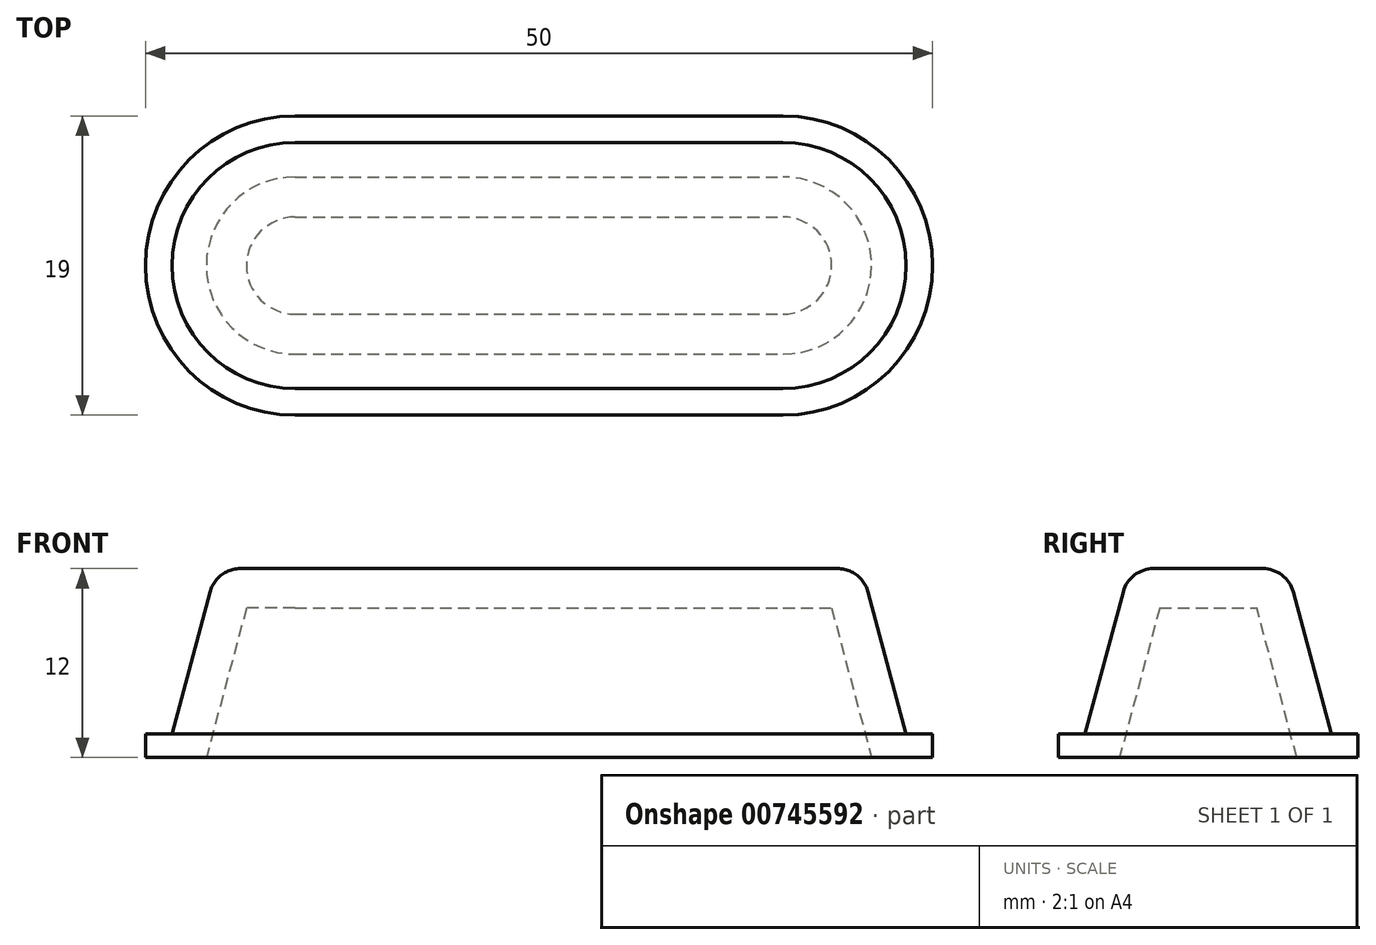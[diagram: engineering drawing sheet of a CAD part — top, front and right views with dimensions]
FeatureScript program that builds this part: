
annotation { "Feature Type Name" : "Feature", "Feature Type Description" : "" }
export const myFeature = defineFeature(function(context is Context, id is Id, definition is map)
    precondition{}
    {
        {
            var Q0;
            Q0=qCreatedBy(makeId("Top.planeOp"),FACE);
            var sketch = newSketch(context, id + "F0", { "sketchPlane" : qUnion([Q0])});
            skLineSegment(sketch, "E0.bottom", {"start": v(25, -9.5) * mm, "end": v(-25, -9.5) * mm, "construction": true});
            skLineSegment(sketch, "E0.top", {"start": v(25, 9.5) * mm, "end": v(-25, 9.5) * mm, "construction": true});
            skLineSegment(sketch, "E0.left", {"start": v(25, -9.5) * mm, "end": v(25, 9.5) * mm, "construction": true});
            skLineSegment(sketch, "E0.right", {"start": v(-25, -9.5) * mm, "end": v(-25, 9.5) * mm, "construction": true});
            skPoint(sketch, "E0.middle", {"position": v(0, 0) * mm});
            skLineSegment(sketch, "E1.bottom", {"start": v(23.5, -8) * mm, "end": v(-23.5, -8) * mm, "construction": true});
            skLineSegment(sketch, "E1.top", {"start": v(23.5, 8) * mm, "end": v(-23.5, 8) * mm, "construction": true});
            skLineSegment(sketch, "E1.left", {"start": v(23.5, -8) * mm, "end": v(23.5, 8) * mm, "construction": true});
            skLineSegment(sketch, "E1.right", {"start": v(-23.5, -8) * mm, "end": v(-23.5, 8) * mm, "construction": true});
            skLineSegment(sketch, "E2", {"start": v(0, 0) * mm, "end": v(-15.5, 0) * mm, "construction": true});
            skLineSegment(sketch, "E3", {"start": v(-15.5, 0) * mm, "end": v(0, 0) * mm, "construction": true});
            skLineSegment(sketch, "E4", {"start": v(0, 0) * mm, "end": v(15.5, 0) * mm, "construction": true});
            skCircle(sketch, "E5", {"center": v(-15.5, 0) * mm, "radius": 8 * mm, "construction": true});
            skCircle(sketch, "E6", {"center": v(15.5, 0) * mm, "radius": 8 * mm, "construction": true});
            skArc(sketch, "E7", {"start": v(-15.5, -8) * mm, "mid": v(-23.5, 0) * mm, "end": v(-15.5, 8) * mm, "construction": true});
            skArc(sketch, "E8", {"start": v(15.5, -8) * mm, "mid": v(23.5, 0) * mm, "end": v(15.5, 8) * mm, "construction": true});
            skLineSegment(sketch, "E9", {"start": v(-15.5, 8) * mm, "end": v(15.5, 8) * mm, "construction": true});
            skLineSegment(sketch, "E10", {"start": v(-15.5, -8) * mm, "end": v(15.5, -8) * mm, "construction": true});
            skArc(sketch, "E11", {"start": v(-15.5, 8) * mm, "mid": v(-23.5, 0) * mm, "end": v(-15.5, -8) * mm});
            skArc(sketch, "E12", {"start": v(15.5, 8) * mm, "mid": v(23.5, 0) * mm, "end": v(15.5, -8) * mm});
            skLineSegment(sketch, "E13", {"start": v(-15.5, -8) * mm, "end": v(15.5, -8) * mm});
            skLineSegment(sketch, "E14", {"start": v(-15.5, 8) * mm, "end": v(15.5, 8) * mm});
            skCircle(sketch, "E15", {"center": v(-15.5, 0) * mm, "radius": 9.5 * mm, "construction": true});
            skCircle(sketch, "E16", {"center": v(15.5, 0) * mm, "radius": 9.5 * mm, "construction": true});
            skArc(sketch, "E17", {"start": v(-15.5, 9.5) * mm, "mid": v(-25, 0) * mm, "end": v(-15.5, -9.5) * mm, "construction": true});
            skArc(sketch, "E18", {"start": v(15.5, 9.5) * mm, "mid": v(25, 0) * mm, "end": v(15.5, -9.5) * mm, "construction": true});
            skArc(sketch, "E19", {"start": v(-15.5, 9.5) * mm, "mid": v(-25, 0) * mm, "end": v(-15.5, -9.5) * mm});
            skArc(sketch, "E20", {"start": v(15.5, 9.5) * mm, "mid": v(25, 0) * mm, "end": v(15.5, -9.5) * mm});
            skLineSegment(sketch, "E21", {"start": v(-15.5, 9.5) * mm, "end": v(15.5, 9.5) * mm});
            skLineSegment(sketch, "E22", {"start": v(-15.5, -9.5) * mm, "end": v(15.5, -9.5) * mm});
            skSolve(sketch);
        }
        {
            var Q0;
            Q0=makeQuery(id+"F0.imprint","IMPRINT",FACE,{"disambiguationData":[TD([[makeQuery(id+"F0.imprint","IMPRINT",EDGE,{"derivedFrom":sQuery(id+"F0.wireOp",EDGE,"E11")}),-1.0]])]});
            var Q1;
            Q1=makeQuery(id+"F0.imprint","IMPRINT",FACE,{"disambiguationData":[TD([[makeQuery(id+"F0.imprint","IMPRINT",EDGE,{"derivedFrom":sQuery(id+"F0.wireOp",EDGE,"E11")}),1.0]])]});
            extrude(context, id + "F1", {"entities" : qUnion([Q0, Q1]), "oppositeDirection" : true, "depth" : 1.5 * mm, "offsetDistance" : 25 * mm});
        }
        {
            var Q0;
            Q0=makeQuery(id+"F1.opExtrude","CAP_FACE",FACE,{"disambiguationData":[OSD([sQuery(id+"F0.wireOp",EDGE,"E19"),sQuery(id+"F0.wireOp",EDGE,"E20"),sQuery(id+"F0.wireOp",EDGE,"E21"),sQuery(id+"F0.wireOp",EDGE,"E22")])],"isStart":true});
            var sketch = newSketch(context, id + "F2", { "sketchPlane" : qUnion([Q0])});
            skLineSegment(sketch, "E23.bottom", {"start": v(25, -9.5) * mm, "end": v(-25, -9.5) * mm, "construction": true});
            skLineSegment(sketch, "E23.top", {"start": v(25, 9.5) * mm, "end": v(-25, 9.5) * mm, "construction": true});
            skLineSegment(sketch, "E23.left", {"start": v(25, -9.5) * mm, "end": v(25, 9.5) * mm, "construction": true});
            skLineSegment(sketch, "E23.right", {"start": v(-25, -9.5) * mm, "end": v(-25, 9.5) * mm, "construction": true});
            skPoint(sketch, "E23.middle", {"position": v(0, 0) * mm});
            skLineSegment(sketch, "E24.bottom", {"start": v(23.5, -8) * mm, "end": v(-23.5, -8) * mm, "construction": true});
            skLineSegment(sketch, "E24.top", {"start": v(23.5, 8) * mm, "end": v(-23.5, 8) * mm, "construction": true});
            skLineSegment(sketch, "E24.left", {"start": v(23.5, -8) * mm, "end": v(23.5, 8) * mm, "construction": true});
            skLineSegment(sketch, "E24.right", {"start": v(-23.5, -8) * mm, "end": v(-23.5, 8) * mm, "construction": true});
            skLineSegment(sketch, "E25", {"start": v(0, 0) * mm, "end": v(-15.5, 0) * mm, "construction": true});
            skLineSegment(sketch, "E26", {"start": v(-15.5, 0) * mm, "end": v(0, 0) * mm, "construction": true});
            skLineSegment(sketch, "E27", {"start": v(0, 0) * mm, "end": v(15.5, 0) * mm, "construction": true});
            skCircle(sketch, "E28", {"center": v(-15.5, 0) * mm, "radius": 8 * mm, "construction": true});
            skCircle(sketch, "E29", {"center": v(15.5, 0) * mm, "radius": 8 * mm, "construction": true});
            skArc(sketch, "E30", {"start": v(-15.5, -8) * mm, "mid": v(-23.5, 0) * mm, "end": v(-15.5, 8) * mm, "construction": true});
            skArc(sketch, "E31", {"start": v(15.5, -8) * mm, "mid": v(23.5, 0) * mm, "end": v(15.5, 8) * mm, "construction": true});
            skLineSegment(sketch, "E32", {"start": v(-15.5, 8) * mm, "end": v(15.5, 8) * mm, "construction": true});
            skLineSegment(sketch, "E33", {"start": v(-15.5, -8) * mm, "end": v(15.5, -8) * mm, "construction": true});
            skArc(sketch, "E34", {"start": v(-15.5, 8) * mm, "mid": v(-23.5, 0) * mm, "end": v(-15.5, -8) * mm});
            skArc(sketch, "E35", {"start": v(15.5, 8) * mm, "mid": v(23.5, 0) * mm, "end": v(15.5, -8) * mm});
            skLineSegment(sketch, "E36", {"start": v(-15.5, -8) * mm, "end": v(15.5, -8) * mm});
            skLineSegment(sketch, "E37", {"start": v(-15.5, 8) * mm, "end": v(15.5, 8) * mm});
            skCircle(sketch, "E38", {"center": v(-15.5, 0) * mm, "radius": 9.5 * mm, "construction": true});
            skCircle(sketch, "E39", {"center": v(15.5, 0) * mm, "radius": 9.5 * mm, "construction": true});
            skArc(sketch, "E40", {"start": v(-15.5, 9.5) * mm, "mid": v(-25, 0) * mm, "end": v(-15.5, -9.5) * mm, "construction": true});
            skArc(sketch, "E41", {"start": v(15.5, 9.5) * mm, "mid": v(25, 0) * mm, "end": v(15.5, -9.5) * mm, "construction": true});
            skArc(sketch, "E42", {"start": v(-15.5, 9.5) * mm, "mid": v(-25, 0) * mm, "end": v(-15.5, -9.5) * mm});
            skArc(sketch, "E43", {"start": v(15.5, 9.5) * mm, "mid": v(25, 0) * mm, "end": v(15.5, -9.5) * mm});
            skLineSegment(sketch, "E44", {"start": v(-15.5, 9.5) * mm, "end": v(15.5, 9.5) * mm});
            skLineSegment(sketch, "E45", {"start": v(-15.5, -9.5) * mm, "end": v(15.5, -9.5) * mm});
            skSolve(sketch);
        }
        {
            var Q0;
            Q0=makeQuery(id+"F2.imprint","IMPRINT",FACE,{"disambiguationData":[TD([[makeQuery(id+"F2.imprint","IMPRINT",EDGE,{"derivedFrom":sQuery(id+"F2.wireOp",EDGE,"E34")}),1.0]])]});
            extrude(context, id + "F3", {"entities" : qUnion([Q0]), "operationType" : NewBodyOperationType.ADD, "depth" : 10.5 * mm, "offsetDistance" : 25 * mm});
        }
        {
            var Q0;
            Q0=makeQuery(id+"F3.opExtrude","CAP_FACE",FACE,{"disambiguationData":[OSD([sQuery(id+"F2.wireOp",EDGE,"E34"),sQuery(id+"F2.wireOp",EDGE,"E35"),sQuery(id+"F2.wireOp",EDGE,"E36"),sQuery(id+"F2.wireOp",EDGE,"E37")])],"isStart":false});
            chamfer(context, id + "F4", {"entities" : qUnion([Q0]), "chamferType" : ChamferType.OFFSET_ANGLE, "width" : 3 * mm, "oppositeDirection" : false, "angle" : 75 * degree, "tangentPropagation" : true});
        }
        {
            var Q0;
            Q0=makeQuery(id+"F1.opExtrude","CAP_FACE",FACE,{"disambiguationData":[OSD([sQuery(id+"F0.wireOp",EDGE,"E19"),sQuery(id+"F0.wireOp",EDGE,"E20"),sQuery(id+"F0.wireOp",EDGE,"E21"),sQuery(id+"F0.wireOp",EDGE,"E22")])],"isStart":false});
            shell(context, id + "F5", {"entities" : qUnion([Q0]), "thickness" : 2.5 * mm});
        }
        {
            var Q0;
            {var subQ0=sQuery(id+"F2.wireOp",EDGE,"E34");Q0=makeQuery(id+"F4.opChamfer","BLEND_EDGE",EDGE,{"blendedFrom":[makeQuery(id+"F3.opExtrude","CAP_EDGE",EDGE,{"disambiguationData":[OSD([subQ0])],"isStart":false}),makeQuery(id+"F3.opExtrude","CAP_FACE",FACE,{"disambiguationData":[OSD([subQ0,sQuery(id+"F2.wireOp",EDGE,"E35"),sQuery(id+"F2.wireOp",EDGE,"E36"),sQuery(id+"F2.wireOp",EDGE,"E37")])],"isStart":false})],"blendedInto":[makeQuery(id+"F3.opExtrude","CAP_FACE",FACE,{"disambiguationData":[OSD([subQ0,sQuery(id+"F2.wireOp",EDGE,"E35"),sQuery(id+"F2.wireOp",EDGE,"E36"),sQuery(id+"F2.wireOp",EDGE,"E37")])],"isStart":false})]});}
            fillet(context, id + "F6", {"entities" : qUnion([Q0]), "radius" : 2 * mm, "tangentPropagation" : true, "allowEdgeOverflow" : false});
        }
    });
